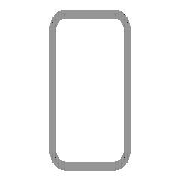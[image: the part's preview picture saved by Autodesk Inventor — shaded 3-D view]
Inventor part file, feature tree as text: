
AUTODESK INVENTOR PART (.ipt)
format: ipt  version: 2025 (Build 290162010, 162A)  size: 153,088 bytes
history: native  units: mm (DEFAULTED — no unit token found)
features: other x3, sketch x2, extrude x1, plane x1
ambient origin geometry x8: Origin, YZ Plane, XZ Plane, XY Plane, X Axis, Y Axis, Z Axis, Center Point
bodies: Solid1 (feature_tree), Body (feature_tree)
feature tree (7):
  other  "Driven Length"
  other  "Start plane"
  other  "End plane"
  extrude  "Extrusion3"  TaperAngle=0.0deg  [1 undecoded]
  sketch  "Sketch3"  dims[d3=350.0mm d4=0.0mm]
  plane  "Work Plane3"
  sketch  "Sketch6"  dims[d7=4.5mm d10=80.0mm d11=40.0mm d12=3.0mm d13=-0.0mm d14=350.0mm d15=40.0mm d16=20.0mm d17=90.0deg d18=350.0mm d22=8.028515mm d23=8.028515mm d24=0.0mm d25=0.0mm]
note: 1 required parameter value undecoded (feature->parameter linkage not recoverable at this tier; creation-order binding heuristic only, values carry confidence <= 0.55)
